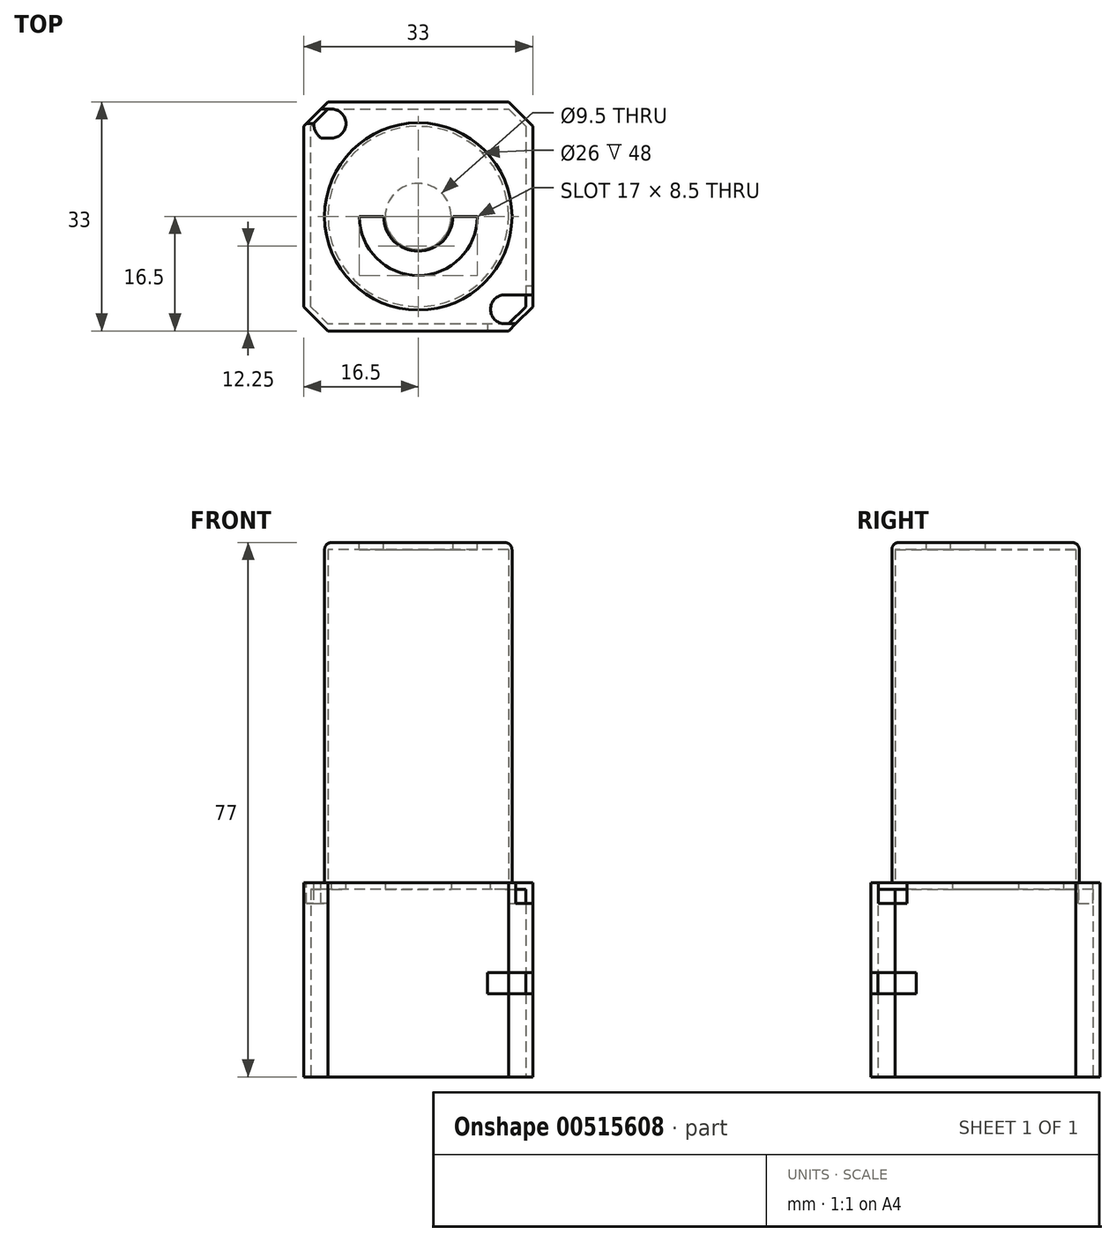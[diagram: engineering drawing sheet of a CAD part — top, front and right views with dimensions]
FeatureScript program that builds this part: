
annotation { "Feature Type Name" : "Feature", "Feature Type Description" : "" }
export const myFeature = defineFeature(function(context is Context, id is Id, definition is map)
    precondition{}
    {
        {
            var Q0;
            Q0=qCreatedBy(makeId("Top.planeOp"),FACE);
            var sketch = newSketch(context, id + "F0", { "sketchPlane" : qUnion([Q0])});
            skLineSegment(sketch, "E0.bottom", {"start": v(-16.5, 16.5) * mm, "end": v(16.5, 16.5) * mm});
            skLineSegment(sketch, "E0.top", {"start": v(-16.5, -16.5) * mm, "end": v(16.5, -16.5) * mm});
            skLineSegment(sketch, "E0.left", {"start": v(-16.5, 16.5) * mm, "end": v(-16.5, -16.5) * mm});
            skLineSegment(sketch, "E0.right", {"start": v(16.5, 16.5) * mm, "end": v(16.5, -16.5) * mm});
            skPoint(sketch, "E0.middle", {"position": v(0, 0) * mm});
            skSolve(sketch);
        }
        {
            var Q0;
            Q0=makeQuery(id+"F0.imprint","IMPRINT",FACE,{"disambiguationData":[TD([[makeQuery(id+"F0.imprint","IMPRINT",EDGE,{"derivedFrom":sQuery(id+"F0.wireOp",EDGE,"E0.bottom")}),-1.0]])]});
            extrude(context, id + "F1", {"entities" : qUnion([Q0]), "depth" : 4 * mm, "offsetDistance" : 25 * mm});
        }
        {
            var Q0;
            Q0=makeQuery(id+"F1.opExtrude","CAP_FACE",FACE,{"disambiguationData":[OSD([sQuery(id+"F0.wireOp",EDGE,"E0.bottom"),sQuery(id+"F0.wireOp",EDGE,"E0.top"),sQuery(id+"F0.wireOp",EDGE,"E0.left"),sQuery(id+"F0.wireOp",EDGE,"E0.right")])],"isStart":false});
            var sketch = newSketch(context, id + "F2", { "sketchPlane" : qUnion([Q0])});
            skLineSegment(sketch, "E1", {"start": v(0, 16.5) * mm, "end": v(-13, 16.5) * mm});
            skLineSegment(sketch, "E2", {"start": v(0, 16.5) * mm, "end": v(13, 16.5) * mm});
            skLineSegment(sketch, "E3", {"start": v(16.5, 0) * mm, "end": v(16.5, 13) * mm});
            skLineSegment(sketch, "E4", {"start": v(16.5, 13) * mm, "end": v(13, 16.5) * mm});
            skLineSegment(sketch, "E5", {"start": v(-16.5, 0) * mm, "end": v(-16.5, 13) * mm});
            skLineSegment(sketch, "E6", {"start": v(-16.5, 0) * mm, "end": v(-16.5, -13) * mm});
            skLineSegment(sketch, "E7", {"start": v(16.5, 0) * mm, "end": v(16.5, -13) * mm});
            skLineSegment(sketch, "E8", {"start": v(0, -16.5) * mm, "end": v(-13, -16.5) * mm});
            skLineSegment(sketch, "E9", {"start": v(0, -16.5) * mm, "end": v(13, -16.5) * mm});
            skLineSegment(sketch, "E10", {"start": v(-16.5, -13) * mm, "end": v(-13, -16.5) * mm});
            skLineSegment(sketch, "E11", {"start": v(-16.5, 13) * mm, "end": v(-13, 16.5) * mm});
            skLineSegment(sketch, "E12", {"start": v(13, -16.5) * mm, "end": v(16.5, -13) * mm});
            skSolve(sketch);
        }
        {
            var Q0;
            {var subQ0=sQuery(id+"F2.wireOp",EDGE,"E4");Q0=makeQuery(id+"F2.imprint","IMPRINT",FACE,{"disambiguationData":[TD([[makeQuery(id+"F2.imprint","IMPRINT",EDGE,{"derivedFrom":subQ0}),-1.0]])]});}
            var Q1;
            {var subQ0=sQuery(id+"F2.wireOp",EDGE,"E10");Q1=makeQuery(id+"F2.imprint","IMPRINT",FACE,{"disambiguationData":[TD([[makeQuery(id+"F2.imprint","IMPRINT",EDGE,{"derivedFrom":subQ0}),-1.0]])]});}
            var Q2;
            {var subQ0=sQuery(id+"F2.wireOp",EDGE,"E12");Q2=makeQuery(id+"F2.imprint","IMPRINT",FACE,{"disambiguationData":[TD([[makeQuery(id+"F2.imprint","IMPRINT",EDGE,{"derivedFrom":subQ0}),-1.0]])]});}
            var Q3;
            {var subQ0=sQuery(id+"F2.wireOp",EDGE,"E11");Q3=makeQuery(id+"F2.imprint","IMPRINT",FACE,{"disambiguationData":[TD([[makeQuery(id+"F2.imprint","IMPRINT",EDGE,{"derivedFrom":subQ0}),1.0]])]});}
            extrude(context, id + "F3", {"entities" : qUnion([Q0, Q1, Q2, Q3]), "operationType" : NewBodyOperationType.REMOVE, "endBound" : BoundingType.THROUGH_ALL, "oppositeDirection" : true, "depth" : 25 * mm, "offsetDistance" : 25 * mm});
        }
        {
            var Q0;
            Q0=makeQuery(id+"F1.opExtrude","CAP_FACE",FACE,{"disambiguationData":[OSD([sQuery(id+"F0.wireOp",EDGE,"E0.bottom"),sQuery(id+"F0.wireOp",EDGE,"E0.top"),sQuery(id+"F0.wireOp",EDGE,"E0.left"),sQuery(id+"F0.wireOp",EDGE,"E0.right")])],"isStart":false});
            var sketch = newSketch(context, id + "F4", { "sketchPlane" : qUnion([Q0])});
            skPoint(sketch, "E13", {"position": v(0, 0) * mm});
            skPoint(sketch, "E13.positionSnap0", {"position": v(16.5, 0) * mm});
            skPoint(sketch, "E13.positionSnap1", {"position": v(0, -16.5) * mm});
            skCircle(sketch, "E14", {"center": v(0, 0) * mm, "radius": 13 * mm});
            skCircle(sketch, "E15", {"center": v(0, 0) * mm, "radius": 13.5 * mm});
            skSolve(sketch);
        }
        {
            var Q0;
            Q0=makeQuery(id+"F4.imprint","IMPRINT",FACE,{"disambiguationData":[TD([[makeQuery(id+"F4.imprint","IMPRINT",EDGE,{"derivedFrom":sQuery(id+"F4.wireOp",EDGE,"E14")}),-1.0]])]});
            extrude(context, id + "F5", {"entities" : qUnion([Q0]), "operationType" : NewBodyOperationType.ADD, "depth" : 48 * mm, "offsetDistance" : 25 * mm});
        }
        {
            var Q0;
            Q0=makeQuery(id+"F5.opExtrude","CAP_FACE",FACE,{"disambiguationData":[OSD([sQuery(id+"F4.wireOp",EDGE,"E14"),sQuery(id+"F4.wireOp",EDGE,"E15")])],"isStart":false});
            var sketch = newSketch(context, id + "F6", { "sketchPlane" : qUnion([Q0])});
            skCircle(sketch, "E16", {"center": v(0, 0) * mm, "radius": 13.5 * mm});
            skSolve(sketch);
        }
        {
            var Q0;
            Q0=makeQuery(id+"F6.imprint","IMPRINT",FACE,{"disambiguationData":[TD([[makeQuery(id+"F6.imprint","IMPRINT",EDGE,{"derivedFrom":sQuery(id+"F6.wireOp",EDGE,"E16")}),1.0]])]});
            var Q1;
            Q1=makeQuery(id+"F6.imprint","IMPRINT",FACE,{"disambiguationData":[TD([[makeQuery(id+"F6.imprint","IMPRINT",EDGE,{"derivedFrom":makeQuery(id+"F5.opExtrude","CAP_EDGE",EDGE,{"disambiguationData":[OSD([sQuery(id+"F4.wireOp",EDGE,"E14")])],"isStart":false})}),1.0]])]});
            extrude(context, id + "F7", {"entities" : qUnion([Q0, Q1]), "operationType" : NewBodyOperationType.ADD, "depth" : 1 * mm, "offsetDistance" : 25 * mm});
        }
        {
            var Q0;
            Q0=makeQuery(id+"F1.opExtrude","CAP_FACE",FACE,{"disambiguationData":[OSD([sQuery(id+"F0.wireOp",EDGE,"E0.bottom"),sQuery(id+"F0.wireOp",EDGE,"E0.top"),sQuery(id+"F0.wireOp",EDGE,"E0.left"),sQuery(id+"F0.wireOp",EDGE,"E0.right")])],"isStart":true});
            var sketch = newSketch(context, id + "F8", { "sketchPlane" : qUnion([Q0])});
            skPoint(sketch, "E17", {"position": v(0, 0) * mm});
            skPoint(sketch, "E17.positionSnap0", {"position": v(16.5, 0) * mm});
            skPoint(sketch, "E17.positionSnap1", {"position": v(0, -16.5) * mm});
            skCircle(sketch, "E18", {"center": v(0, 0) * mm, "radius": 4.75 * mm});
            skCircle(sketch, "E19", {"center": v(0, 0) * mm, "radius": 5.25 * mm});
            skSolve(sketch);
        }
        {
            var Q0;
            Q0=makeQuery(id+"F8.imprint","IMPRINT",FACE,{"disambiguationData":[TD([[makeQuery(id+"F8.imprint","IMPRINT",EDGE,{"derivedFrom":sQuery(id+"F8.wireOp",EDGE,"E18")}),1.0]])]});
            extrude(context, id + "F9", {"entities" : qUnion([Q0]), "operationType" : NewBodyOperationType.REMOVE, "oppositeDirection" : true, "depth" : 25 * mm, "offsetDistance" : 25 * mm});
        }
        {
            var Q0;
            Q0=makeQuery(id+"F1.opExtrude","CAP_FACE",FACE,{"disambiguationData":[OSD([sQuery(id+"F0.wireOp",EDGE,"E0.bottom"),sQuery(id+"F0.wireOp",EDGE,"E0.top"),sQuery(id+"F0.wireOp",EDGE,"E0.left"),sQuery(id+"F0.wireOp",EDGE,"E0.right")])],"isStart":true});
            extrude(context, id + "F10", {"entities" : qUnion([Q0]), "operationType" : NewBodyOperationType.ADD, "depth" : 24 * mm, "offsetDistance" : 25 * mm});
        }
        {
            var Q0;
            Q0=makeQuery(id+"F7.opExtrude","CAP_FACE",FACE,{"disambiguationData":[OSD([sQuery(id+"F6.wireOp",EDGE,"E16")])],"isStart":false});
            var sketch = newSketch(context, id + "F11", { "sketchPlane" : qUnion([Q0])});
            skCircle(sketch, "E20", {"center": v(0, 0) * mm, "radius": 8.5 * mm});
            skLineSegment(sketch, "E21", {"start": v(0, 0) * mm, "end": v(-8.5, 0) * mm});
            skLineSegment(sketch, "E22", {"start": v(-8.5, 0) * mm, "end": v(8.5, 0) * mm});
            skCircle(sketch, "E23", {"center": v(0, 0) * mm, "radius": 5 * mm});
            skSolve(sketch);
        }
        {
            var Q0;
            {var subQ0=sQuery(id+"F11.wireOp",EDGE,"E22");var subQ1=sQuery(id+"F11.wireOp",EDGE,"E20");var subQ2=makeQuery(id+"F11.imprint","INTERSECT",VERTEX,{"disambiguationData":[OD(0.0)],"derivedFrom":[subQ1,subQ0]});Q0=makeQuery(id+"F11.imprint","IMPRINT",FACE,{"disambiguationData":[TD([[makeQuery(id+"F11.imprint","IMPRINT",EDGE,{"disambiguationData":[TD([[subQ2,1.0]])],"derivedFrom":subQ1}),1.0]])]});}
            extrude(context, id + "F12", {"entities" : qUnion([Q0]), "operationType" : NewBodyOperationType.REMOVE, "oppositeDirection" : true, "depth" : 25 * mm, "offsetDistance" : 25 * mm});
        }
        {
            var Q0;
            Q0=makeQuery(id+"F7.opExtrude","CAP_EDGE",EDGE,{"disambiguationData":[OSD([sQuery(id+"F6.wireOp",EDGE,"E16")])],"isStart":false});
            fillet(context, id + "F13", {"entities" : qUnion([Q0]), "radius" : 1 * mm, "tangentPropagation" : true, "allowEdgeOverflow" : false});
        }
        {
            var Q0;
            {var subQ0=sQuery(id+"F0.wireOp",EDGE,"E0.left");var subQ1=sQuery(id+"F0.wireOp",EDGE,"E0.top");var subQ2=sQuery(id+"F0.wireOp",EDGE,"E0.right");var subQ3=sQuery(id+"F0.wireOp",EDGE,"E0.bottom");Q0=makeQuery(id+"F5.boolean.opBoolean","SPLIT",FACE,{"disambiguationData":[TD([makeQuery(id+"F1.opExtrude","SWEPT_FACE",FACE,{"disambiguationData":[OSD([subQ3])]})])],"derivedFrom":makeQuery(id+"F1.opExtrude","CAP_FACE",FACE,{"disambiguationData":[OSD([subQ3,subQ1,subQ0,subQ2])],"isStart":false})});}
            var sketch = newSketch(context, id + "F14", { "sketchPlane" : qUnion([Q0])});
            skLineSegment(sketch, "E24", {"start": v(16.5, -13) * mm, "end": v(16.5, -12) * mm});
            skPoint(sketch, "E25", {"position": v(16.11, -13.39) * mm});
            skLineSegment(sketch, "E26", {"start": v(16.11, -13.39) * mm, "end": v(14.03, -13.39) * mm});
            skLineSegment(sketch, "E27", {"start": v(12.47, -13.39) * mm, "end": v(10.56, -13.39) * mm});
            skLineSegment(sketch, "E28", {"start": v(14.03, -13.39) * mm, "end": v(12.5, -13.38) * mm});
            skCircle(sketch, "E29", {"center": v(12.5, -13.38) * mm, "radius": 1.56 * mm});
            skLineSegment(sketch, "E30", {"start": v(12.5, -13.38) * mm, "end": v(12.5, -16.5) * mm});
            skCircle(sketch, "E31", {"center": v(12.5, -13.38) * mm, "radius": 2.08 * mm});
            skPoint(sketch, "E32", {"position": v(12.5, -11.3) * mm});
            skPoint(sketch, "E33", {"position": v(12.5, -15.46) * mm});
            skLineSegment(sketch, "E34", {"start": v(12.5, -15.46) * mm, "end": v(14.04, -15.46) * mm});
            skLineSegment(sketch, "E35", {"start": v(12.5, -11.3) * mm, "end": v(16.5, -11.3) * mm});
            skSolve(sketch);
        }
        {
            var Q0;
            {var subQ0=sQuery(id+"F14.wireOp",EDGE,"F2J8uAUn-3WnW-PfaH-BXMC-vPAdsd7hCkW2");var subQ1=sQuery(id+"F14.wireOp",EDGE,"E27");var subQ2=makeQuery(id+"F14.imprint","INTERSECT",VERTEX,{"derivedFrom":[subQ1,subQ0]});Q0=makeQuery(id+"F14.imprint","IMPRINT",FACE,{"disambiguationData":[TD([[makeQuery(id+"F14.imprint","IMPRINT",EDGE,{"disambiguationData":[TD([[subQ2,-1.0]])],"derivedFrom":subQ1}),1.0]])]});}
            var Q1;
            {var subQ1=sQuery(id+"F14.wireOp",EDGE,"E26");var subQ3=sQuery(id+"F14.wireOp",EDGE,"E29");var subQ4=makeQuery(id+"F14.imprint","INTERSECT",VERTEX,{"derivedFrom":[subQ1,subQ3]});Q1=makeQuery(id+"F14.imprint","IMPRINT",FACE,{"disambiguationData":[TD([[makeQuery(id+"F14.imprint","IMPRINT",EDGE,{"disambiguationData":[TD([[subQ4,1.0]])],"derivedFrom":subQ3}),1.0]])]});}
            var Q2;
            {var subQ5=sQuery(id+"F14.wireOp",EDGE,"E28");Q2=makeQuery(id+"F14.imprint","IMPRINT",FACE,{"disambiguationData":[TD([[makeQuery(id+"F14.imprint","IMPRINT",EDGE,{"derivedFrom":subQ5}),-1.0]])]});}
            extrude(context, id + "F15", {"entities" : qUnion([Q0, Q1, Q2]), "operationType" : NewBodyOperationType.REMOVE, "endBound" : BoundingType.THROUGH_ALL, "oppositeDirection" : true, "depth" : 25 * mm, "offsetDistance" : 25 * mm});
        }
        {
            var Q0;
            {var subQ3=sQuery(id+"F14.wireOp",EDGE,"E29");var subQ5=makeQuery(id+"F14.imprint","IMPRINT",VERTEX,{"derivedFrom":subQ3});Q0=makeQuery(id+"F14.imprint","IMPRINT",FACE,{"disambiguationData":[TD([[makeQuery(id+"F14.imprint","IMPRINT",EDGE,{"disambiguationData":[TD([[subQ5,-1.0]])],"derivedFrom":subQ3}),-1.0]])]});}
            var Q1;
            {var subQ0=sQuery(id+"F14.wireOp",EDGE,"E31");var subQ1=sQuery(id+"F14.wireOp",EDGE,"E26");var subQ2=makeQuery(id+"F14.imprint","INTERSECT",VERTEX,{"derivedFrom":[subQ1,subQ0]});Q1=makeQuery(id+"F14.imprint","IMPRINT",FACE,{"disambiguationData":[TD([[makeQuery(id+"F14.imprint","IMPRINT",EDGE,{"disambiguationData":[TD([[subQ2,-1.0]])],"derivedFrom":subQ1}),1.0]])]});}
            var Q2;
            {var subQ5=sQuery(id+"F14.wireOp",EDGE,"E34");Q2=makeQuery(id+"F14.imprint","IMPRINT",FACE,{"disambiguationData":[TD([[makeQuery(id+"F14.imprint","IMPRINT",EDGE,{"derivedFrom":subQ5}),1.0]])]});}
            var Q3;
            {var subQ6=sQuery(id+"F14.wireOp",EDGE,"E24");Q3=makeQuery(id+"F14.imprint","IMPRINT",FACE,{"disambiguationData":[TD([[makeQuery(id+"F14.imprint","IMPRINT",EDGE,{"derivedFrom":subQ6}),-1.0]])]});}
            extrude(context, id + "F16", {"entities" : qUnion([Q0, Q1, Q2, Q3]), "operationType" : NewBodyOperationType.REMOVE, "oppositeDirection" : true, "depth" : 3 * mm, "offsetDistance" : 25 * mm});
        }
        {
            var Q0;
            {var subQ0=sQuery(id+"F0.wireOp",EDGE,"E0.left");var subQ1=sQuery(id+"F0.wireOp",EDGE,"E0.top");var subQ2=sQuery(id+"F0.wireOp",EDGE,"E0.right");var subQ3=sQuery(id+"F0.wireOp",EDGE,"E0.bottom");Q0=makeQuery(id+"F5.boolean.opBoolean","SPLIT",FACE,{"disambiguationData":[TD([makeQuery(id+"F1.opExtrude","SWEPT_FACE",FACE,{"disambiguationData":[OSD([subQ3])]})])],"derivedFrom":makeQuery(id+"F1.opExtrude","CAP_FACE",FACE,{"disambiguationData":[OSD([subQ3,subQ1,subQ0,subQ2])],"isStart":false})});}
            var sketch = newSketch(context, id + "F17", { "sketchPlane" : qUnion([Q0])});
            skLineSegment(sketch, "E36", {"start": v(-13, 16.5) * mm, "end": v(-12.49, 16.5) * mm});
            skLineSegment(sketch, "E37", {"start": v(-12.49, 16.5) * mm, "end": v(-12.49, 15.46) * mm});
            skLineSegment(sketch, "E38", {"start": v(-12.49, 15.46) * mm, "end": v(-12.49, 13.4) * mm});
            skLineSegment(sketch, "E39", {"start": v(-12.49, 13.4) * mm, "end": v(-16.1, 13.4) * mm});
            skCircle(sketch, "E40", {"center": v(-12.49, 13.4) * mm, "radius": 1.56 * mm});
            skCircle(sketch, "E41", {"center": v(-12.49, 13.4) * mm, "radius": 2.08 * mm});
            skLineSegment(sketch, "E42", {"start": v(-12.49, 15.46) * mm, "end": v(-14.04, 15.46) * mm});
            skLineSegment(sketch, "E43", {"start": v(-12.49, 11.31) * mm, "end": v(-16.5, 11.31) * mm});
            skCircle(sketch, "E44", {"center": v(-12.49, 13.4) * mm, "radius": 2.58 * mm});
            skSolve(sketch);
        }
        {
            var Q0;
            {var subQ0=sQuery(id+"F17.wireOp",EDGE,"E39");var subQ1=sQuery(id+"F17.wireOp",EDGE,"E38");var subQ2=makeQuery(id+"F17.imprint","INTERSECT",VERTEX,{"derivedFrom":[subQ1,subQ0]});Q0=makeQuery(id+"F17.imprint","IMPRINT",FACE,{"disambiguationData":[TD([[makeQuery(id+"F17.imprint","IMPRINT",EDGE,{"disambiguationData":[TD([[subQ2,1.0]])],"derivedFrom":subQ1}),1.0]])]});}
            var Q1;
            {var subQ0=sQuery(id+"F17.wireOp",EDGE,"E39");var subQ1=sQuery(id+"F17.wireOp",EDGE,"E38");var subQ2=makeQuery(id+"F17.imprint","INTERSECT",VERTEX,{"derivedFrom":[subQ1,subQ0]});Q1=makeQuery(id+"F17.imprint","IMPRINT",FACE,{"disambiguationData":[TD([[makeQuery(id+"F17.imprint","IMPRINT",EDGE,{"disambiguationData":[TD([[subQ2,1.0]])],"derivedFrom":subQ1}),-1.0]])]});}
            extrude(context, id + "F18", {"entities" : qUnion([Q0, Q1]), "operationType" : NewBodyOperationType.REMOVE, "endBound" : BoundingType.THROUGH_ALL, "oppositeDirection" : true, "depth" : 25 * mm, "offsetDistance" : 25 * mm});
        }
        {
            var Q0;
            {var subQ1=sQuery(id+"F17.wireOp",EDGE,"E39");var subQ5=sQuery(id+"F17.wireOp",EDGE,"E40");var subQ6=makeQuery(id+"F17.imprint","INTERSECT",VERTEX,{"derivedFrom":[subQ1,subQ5]});Q0=makeQuery(id+"F17.imprint","IMPRINT",FACE,{"disambiguationData":[TD([[makeQuery(id+"F17.imprint","IMPRINT",EDGE,{"disambiguationData":[TD([[subQ6,-1.0]])],"derivedFrom":subQ1}),-1.0]])]});}
            var Q1;
            {var subQ0=sQuery(id+"F17.wireOp",EDGE,"E39");var subQ1=makeQuery(id+"F3.boolean.opBoolean","COPY",EDGE,{"derivedFrom":makeQuery(id+"F3.opExtrude","CAP_EDGE",EDGE,{"disambiguationData":[OSD([sQuery(id+"F2.wireOp",EDGE,"E11")])],"isStart":true})});var subQ2=makeQuery(id+"F17.imprint","INTERSECT",VERTEX,{"derivedFrom":[subQ1,subQ0]});Q1=makeQuery(id+"F17.imprint","IMPRINT",FACE,{"disambiguationData":[TD([[makeQuery(id+"F17.imprint","IMPRINT",EDGE,{"disambiguationData":[TD([[subQ2,1.0]])],"derivedFrom":subQ0}),-1.0]])]});}
            var Q2;
            {var subQ0=sQuery(id+"F17.wireOp",EDGE,"E40");var subQ3=sQuery(id+"F17.wireOp",EDGE,"E39");var subQ4=makeQuery(id+"F17.imprint","INTERSECT",VERTEX,{"derivedFrom":[subQ3,subQ0]});Q2=makeQuery(id+"F17.imprint","IMPRINT",FACE,{"disambiguationData":[TD([[makeQuery(id+"F17.imprint","IMPRINT",EDGE,{"disambiguationData":[TD([[subQ4,-1.0]])],"derivedFrom":subQ3}),1.0]])]});}
            var Q3;
            {var subQ1=makeQuery(id+"F3.boolean.opBoolean","COPY",EDGE,{"derivedFrom":makeQuery(id+"F3.opExtrude","CAP_EDGE",EDGE,{"disambiguationData":[OSD([sQuery(id+"F2.wireOp",EDGE,"E11")])],"isStart":true})});var subQ3=sQuery(id+"F17.wireOp",EDGE,"E39");var subQ4=makeQuery(id+"F17.imprint","INTERSECT",VERTEX,{"derivedFrom":[subQ1,subQ3]});Q3=makeQuery(id+"F17.imprint","IMPRINT",FACE,{"disambiguationData":[TD([[makeQuery(id+"F17.imprint","IMPRINT",EDGE,{"disambiguationData":[TD([[subQ4,1.0]])],"derivedFrom":subQ3}),1.0]])]});}
            var Q4;
            {var subQ0=sQuery(id+"F17.wireOp",EDGE,"E41");var subQ1=sQuery(id+"F17.wireOp",EDGE,"E39");var subQ2=makeQuery(id+"F17.imprint","INTERSECT",VERTEX,{"derivedFrom":[subQ1,subQ0]});Q4=makeQuery(id+"F17.imprint","IMPRINT",FACE,{"disambiguationData":[TD([[makeQuery(id+"F17.imprint","IMPRINT",EDGE,{"disambiguationData":[TD([[subQ2,-1.0]])],"derivedFrom":subQ1}),1.0]])]});}
            var Q5;
            {var subQ5=sQuery(id+"F17.wireOp",EDGE,"E41");var subQ7=sQuery(id+"F17.wireOp",EDGE,"E39");var subQ8=makeQuery(id+"F17.imprint","INTERSECT",VERTEX,{"derivedFrom":[subQ7,subQ5]});Q5=makeQuery(id+"F17.imprint","IMPRINT",FACE,{"disambiguationData":[TD([[makeQuery(id+"F17.imprint","IMPRINT",EDGE,{"disambiguationData":[TD([[subQ8,-1.0]])],"derivedFrom":subQ7}),-1.0]])]});}
            extrude(context, id + "F19", {"entities" : qUnion([Q0, Q1, Q2, Q3, Q4, Q5]), "operationType" : NewBodyOperationType.REMOVE, "oppositeDirection" : true, "depth" : 3 * mm, "offsetDistance" : 25 * mm});
        }
        {
            var Q0;
            {var subQ0=sQuery(id+"F0.wireOp",EDGE,"E0.right");Q0=makeQuery(id+"F10.boolean.opBoolean","MERGE",FACE,{"derivedFrom":[makeQuery(id+"F1.opExtrude","SWEPT_FACE",FACE,{"disambiguationData":[OSD([subQ0])]}),makeQuery(id+"F10.opExtrude","SWEPT_FACE",FACE,{"disambiguationData":[OSD([subQ0])]})]});}
            var sketch = newSketch(context, id + "F20", { "sketchPlane" : qUnion([Q0])});
            skLineSegment(sketch, "E45", {"start": v(-13, -24) * mm, "end": v(-13, -12) * mm});
            skLineSegment(sketch, "E46", {"start": v(-13, -9) * mm, "end": v(-10, -9) * mm});
            skLineSegment(sketch, "E47", {"start": v(-13, -12) * mm, "end": v(-10, -12) * mm});
            skLineSegment(sketch, "E48", {"start": v(-10, -12) * mm, "end": v(-10, -9) * mm});
            skSolve(sketch);
        }
        {
            var Q0;
            {var subQ0=sQuery(id+"F2.wireOp",EDGE,"E12");Q0=makeQuery(id+"F10.boolean.opBoolean","MERGE",FACE,{"derivedFrom":[makeQuery(id+"F3.boolean.opBoolean","COPY",FACE,{"derivedFrom":makeQuery(id+"F3.opExtrude","SWEPT_FACE",FACE,{"disambiguationData":[OSD([subQ0])]})}),makeQuery(id+"F10.opExtrude","SWEPT_FACE",FACE,{"disambiguationData":[OSD([sQuery(id+"F0.wireOp",EDGE,"E0.bottom"),sQuery(id+"F0.wireOp",EDGE,"E0.top"),sQuery(id+"F0.wireOp",EDGE,"E0.left"),sQuery(id+"F0.wireOp",EDGE,"E0.right"),subQ0])]})]});}
            var sketch = newSketch(context, id + "F21", { "sketchPlane" : qUnion([Q0])});
            skLineSegment(sketch, "E49", {"start": v(2.47, -24) * mm, "end": v(2.47, -12) * mm});
            skLineSegment(sketch, "E50", {"start": v(-2.47, -24) * mm, "end": v(-2.47, -12) * mm});
            skLineSegment(sketch, "E51", {"start": v(-2.47, -12) * mm, "end": v(2.47, -12) * mm});
            skLineSegment(sketch, "E52", {"start": v(2.47, -9) * mm, "end": v(-2.47, -9) * mm});
            skSolve(sketch);
        }
        {
            var Q0;
            {var subQ0=sQuery(id+"F0.wireOp",EDGE,"E0.top");Q0=makeQuery(id+"F10.boolean.opBoolean","MERGE",FACE,{"derivedFrom":[makeQuery(id+"F1.opExtrude","SWEPT_FACE",FACE,{"disambiguationData":[OSD([subQ0])]}),makeQuery(id+"F10.opExtrude","SWEPT_FACE",FACE,{"disambiguationData":[OSD([subQ0])]})]});}
            var sketch = newSketch(context, id + "F22", { "sketchPlane" : qUnion([Q0])});
            skLineSegment(sketch, "E53", {"start": v(13, -24) * mm, "end": v(13, -12) * mm});
            skLineSegment(sketch, "E54", {"start": v(13, -9) * mm, "end": v(10, -9) * mm});
            skLineSegment(sketch, "E55", {"start": v(13, -12) * mm, "end": v(10, -12) * mm});
            skLineSegment(sketch, "E56", {"start": v(10, -12) * mm, "end": v(10, -9) * mm});
            skSolve(sketch);
        }
        {
            var Q0;
            {var subQ0=sQuery(id+"F21.wireOp",EDGE,"E51");Q0=makeQuery(id+"F21.imprint","IMPRINT",FACE,{"disambiguationData":[TD([[makeQuery(id+"F21.imprint","IMPRINT",EDGE,{"derivedFrom":subQ0}),1.0]])]});}
            extrude(context, id + "F23", {"entities" : qUnion([Q0]), "operationType" : NewBodyOperationType.REMOVE, "oppositeDirection" : true, "depth" : 25 * mm, "offsetDistance" : 25 * mm});
        }
        {
            var Q0;
            {var subQ0=sQuery(id+"F22.wireOp",EDGE,"E54");Q0=makeQuery(id+"F22.imprint","IMPRINT",FACE,{"disambiguationData":[TD([[makeQuery(id+"F22.imprint","IMPRINT",EDGE,{"derivedFrom":subQ0}),1.0]])]});}
            extrude(context, id + "F24", {"entities" : qUnion([Q0]), "operationType" : NewBodyOperationType.REMOVE, "oppositeDirection" : true, "depth" : 25 * mm, "offsetDistance" : 25 * mm});
        }
        {
            var Q0;
            {var subQ0=sQuery(id+"F20.wireOp",EDGE,"E46");Q0=makeQuery(id+"F20.imprint","IMPRINT",FACE,{"disambiguationData":[TD([[makeQuery(id+"F20.imprint","IMPRINT",EDGE,{"derivedFrom":subQ0}),-1.0]])]});}
            extrude(context, id + "F25", {"entities" : qUnion([Q0]), "operationType" : NewBodyOperationType.REMOVE, "oppositeDirection" : true, "depth" : 25 * mm, "offsetDistance" : 25 * mm});
        }
        {
            var Q0;
            Q0=makeQuery(id+"F10.opExtrude","CAP_FACE",FACE,{"disambiguationData":[OSD([sQuery(id+"F0.wireOp",EDGE,"E0.bottom"),sQuery(id+"F0.wireOp",EDGE,"E0.top"),sQuery(id+"F0.wireOp",EDGE,"E0.left"),sQuery(id+"F0.wireOp",EDGE,"E0.right")])],"isStart":false});
            var sketch = newSketch(context, id + "F26", { "sketchPlane" : qUnion([Q0])});
            skLineSegment(sketch, "E57", {"start": v(-13, 16.5) * mm, "end": v(-13, 15.5) * mm});
            skLineSegment(sketch, "E58", {"start": v(13, 16.5) * mm, "end": v(13, 15.5) * mm});
            skLineSegment(sketch, "E59", {"start": v(13, 15.5) * mm, "end": v(-13, 15.5) * mm});
            skLineSegment(sketch, "E60", {"start": v(16.5, 13) * mm, "end": v(15.5, 13) * mm});
            skLineSegment(sketch, "E61", {"start": v(15.5, 13) * mm, "end": v(13, 15.5) * mm});
            skLineSegment(sketch, "E62", {"start": v(16.5, -13) * mm, "end": v(15.5, -13) * mm});
            skLineSegment(sketch, "E63", {"start": v(13, -16.5) * mm, "end": v(13, -15.5) * mm});
            skLineSegment(sketch, "E64", {"start": v(-13, -16.5) * mm, "end": v(-13, -15.5) * mm});
            skLineSegment(sketch, "E65", {"start": v(-16.5, -13) * mm, "end": v(-15.5, -13) * mm});
            skLineSegment(sketch, "E66", {"start": v(-16.5, 13) * mm, "end": v(-15.5, 13) * mm});
            skLineSegment(sketch, "E67", {"start": v(-15.5, 13) * mm, "end": v(-13, 15.5) * mm});
            skLineSegment(sketch, "E68", {"start": v(-15.5, 13) * mm, "end": v(-15.5, -13) * mm});
            skLineSegment(sketch, "E69", {"start": v(-13, -15.5) * mm, "end": v(-15.5, -13) * mm});
            skLineSegment(sketch, "E70", {"start": v(-13, -15.5) * mm, "end": v(13, -15.5) * mm});
            skLineSegment(sketch, "E71", {"start": v(13, -15.5) * mm, "end": v(15.5, -13) * mm});
            skLineSegment(sketch, "E72", {"start": v(15.5, -13) * mm, "end": v(15.5, 13) * mm});
            skSolve(sketch);
        }
        {
            var Q0;
            Q0=makeQuery(id+"F26.imprint","IMPRINT",FACE,{"disambiguationData":[TD([[makeQuery(id+"F26.imprint","IMPRINT",EDGE,{"derivedFrom":sQuery(id+"F26.wireOp",EDGE,"E59")}),1.0]])]});
            extrude(context, id + "F27", {"entities" : qUnion([Q0]), "operationType" : NewBodyOperationType.REMOVE, "oppositeDirection" : true, "depth" : 27 * mm, "offsetDistance" : 25 * mm});
        }
    });
